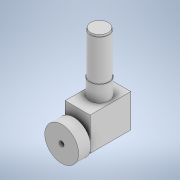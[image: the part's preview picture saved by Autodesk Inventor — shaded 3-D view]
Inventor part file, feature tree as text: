
AUTODESK INVENTOR PART (.ipt)
format: ipt  version: 2020 (Build 240168000, 168)  size: 165,888 bytes
history: native  units: mm
features: extrude x8, sketch x8
ambient origin geometry x8: Origin, YZ Plane, XZ Plane, XY Plane, X Axis, Y Axis, Z Axis, Center Point
bodies: Solide1 (feature_tree)
feature tree (16):
  extrude  "Extrusion1"  Depth=40.2mm
  extrude  "Extrusion2"  Depth=65.7mm
  extrude  "Extrusion3"  Depth=10.2mm TaperAngle=0.0deg
  extrude  "Extrusion4"  Depth=43.4mm
  extrude  "Extrusion5"  Depth=12.0mm TaperAngle=0.0deg
  extrude  "Extrusion6"  Depth=14.2mm
  extrude  "Extrusion7"  Depth=19.2mm
  extrude  "Extrusion8"  Depth=31.65mm
  sketch  "Esquisse1"
  sketch  "Esquisse2"
  sketch  "Esquisse3"
  sketch  "Esquisse4"
  sketch  "Esquisse5"
  sketch  "Esquisse6"
  sketch  "Esquisse7"
  sketch  "Esquisse8"
